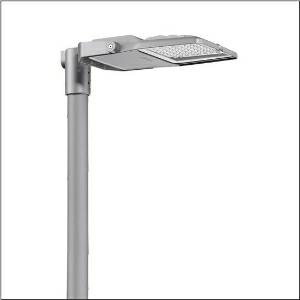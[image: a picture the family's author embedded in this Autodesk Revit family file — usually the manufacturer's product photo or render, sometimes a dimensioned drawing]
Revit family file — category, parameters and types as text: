
# Revit family: floodlight_fl_21_iq_mini___pl52_5xa7771b2d3a_cd8f
name_source: partatom
category: Lighting Fixtures
units: mm (PartAtom-declared; Revit-internal decimal feet)

## family parameters
Cut with Voids When Loaded = No
Host = Face
Light Source = No
Part Type = Normal
Room Calculation Point = No
Round Connector Dimension = Use Diameter
Shared = No

## types (1)
- --- (1 x LED, 6240 lm, 45.5 W, 3000K)
    Apparent Load = 46 VA
    CIE Flux Codes = 26 60 98 100 100
    Color Rendering = 70
    Color Temperature = 3000K
    Default Elevation = 1800 mm
    Description = Floodlight FL 21 iQ mini, floodlight, primary light control with lens, of PMMA, primary optical cover: protective disc, of toughened safety glass, transparent, light distribution: PL52, light emission: direct distribution, installation type: surface-mounted, lamps: LED, High Power LED, rated values: 6.240lm | 45,5W | 137,1lm/W (begin service life); end service life: 6.240lm | 48W; at 50% lumin. flux: 3.120lm | 21,5W | 145,1lm/W, colour temperature: 3000K, colour rendering: CRI > 70, light colour: 730, light setting 1 begin service life: 100% | 6.240lm | 45,5W | 137,1lm/W | 3.000K, light setting 1 end service life: 48W, further light settings possible, control: Auto-Match, Temp-Guard, Lumen-Switch, Night-Set, Smart-Wire, Light-Fading, Desk-Remote (wireless, voltage-free reading and setting of iQ features in the workshop via application-optimized NFC function/RFID function), optimised constant luminous flux control (CLO 2.0), pre-setting: linear dimming characteristic, with terminal, 6-pole, mains connection: 220..240V, AC, 50/60Hz, luminaire housing, of diecast aluminium, powder-coated, SITECO metallic grey (DB 702S), corrosivity category C5 mid according to DIN EN ISO 12944suitable for swimming poolschlorine-resistant, sealing non-destructively replaceable, please order mast flange separately, mast bracket, of steel, galvanised, powder-coated, SITECO metallic grey (DB 702S), protection rating (complete): IP66, insulation class (complete): insulation class II (safety insulation), certification: CE, ENEC, VDE, protection symbol: D, impact resistance: IK08, permissible operating ambient temperature: -40..+40°C, permissible operating ambient temperature for outdoor applications: -40..+50°C, standard: DIN EN 12944, LABS conformity tested according to VDMA 24364:2018-05, packaging unit: 1 piece

Light Distribution: PL52
    Height = 70 mm
    Lamp = 1 x LED
    Lamp Light Flux = 6240 lm
    Lamp Power = 45.5 W
    Lamp count = 1
    Length = 485 mm
    Luminous efficacy = 137 lm/W
    Manufacturer = Siteco
    ModVariant = No
    Model = 5XA7771B2D3A
    Number of Poles = 1
    OnlyDefault = Yes
    Power Factor = 1
    Product Name = Floodlight FL 21 iQ mini | PL52
    Product group = floodlight | pylon annexe
    ProductGroupID = 6201
    Protection Class = Protection class II
    Protection Degree = IP 66
    RLX_Detail_Level = 1
    RLX_Emergency_Light_Flux = 0 lm
    RLX_Emergency_Type = 0
    RLX_Emergency_Type_DB = No
    RlxData = <blob elided: 101745 chars, md5=44cdacea>
    Socket = socket
    Standby Power = 0 W
    System Light Flux = 6240 lm
    System Power = 46 W
    Type Comments = factory setting: luminous flux: 100 % | dim-lin: 254 | 463 mA
    Type Image = l_1007125.jpg
    URL = http://relux.com
    VarID = @adj_164565
    Voltage = 0 V
    Weight = 0.00 kg
    Width = 337 mm

## geometry (parser evidence)
native form markers: Blend x4, Sweep x11
no freeform markers — native parametric forms only
